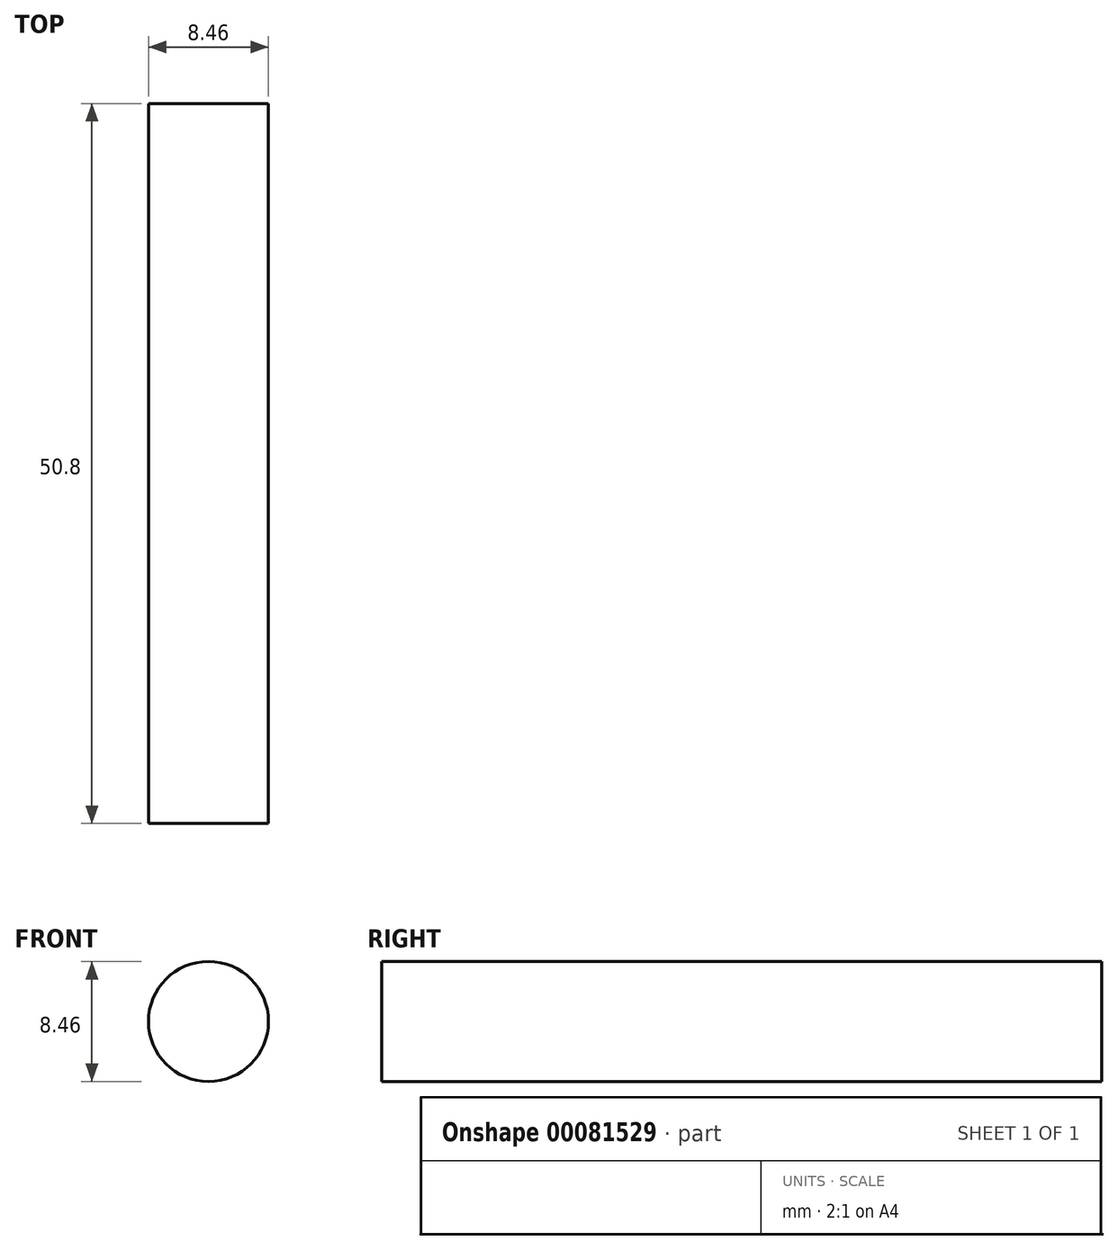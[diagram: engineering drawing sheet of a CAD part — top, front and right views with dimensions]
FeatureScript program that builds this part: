
annotation { "Feature Type Name" : "Feature", "Feature Type Description" : "" }
export const myFeature = defineFeature(function(context is Context, id is Id, definition is map)
    precondition{}
    {
        {
            var Q0;
            Q0=qCreatedBy(makeId("Front.planeOp"),FACE);
            var sketch = newSketch(context, id + "F0", { "sketchPlane" : qUnion([Q0])});
            skCircle(sketch, "E0", {"center": v(0, 0) * mm, "radius": 4.23 * mm});
            skSolve(sketch);
        }
        {
            var Q0;
            Q0 = qSketchRegion(id + "F0", true);
            extrude(context, id + "F1", {"entities" : qUnion([Q0]), "depth" : 50.8 * mm});
        }
    });
